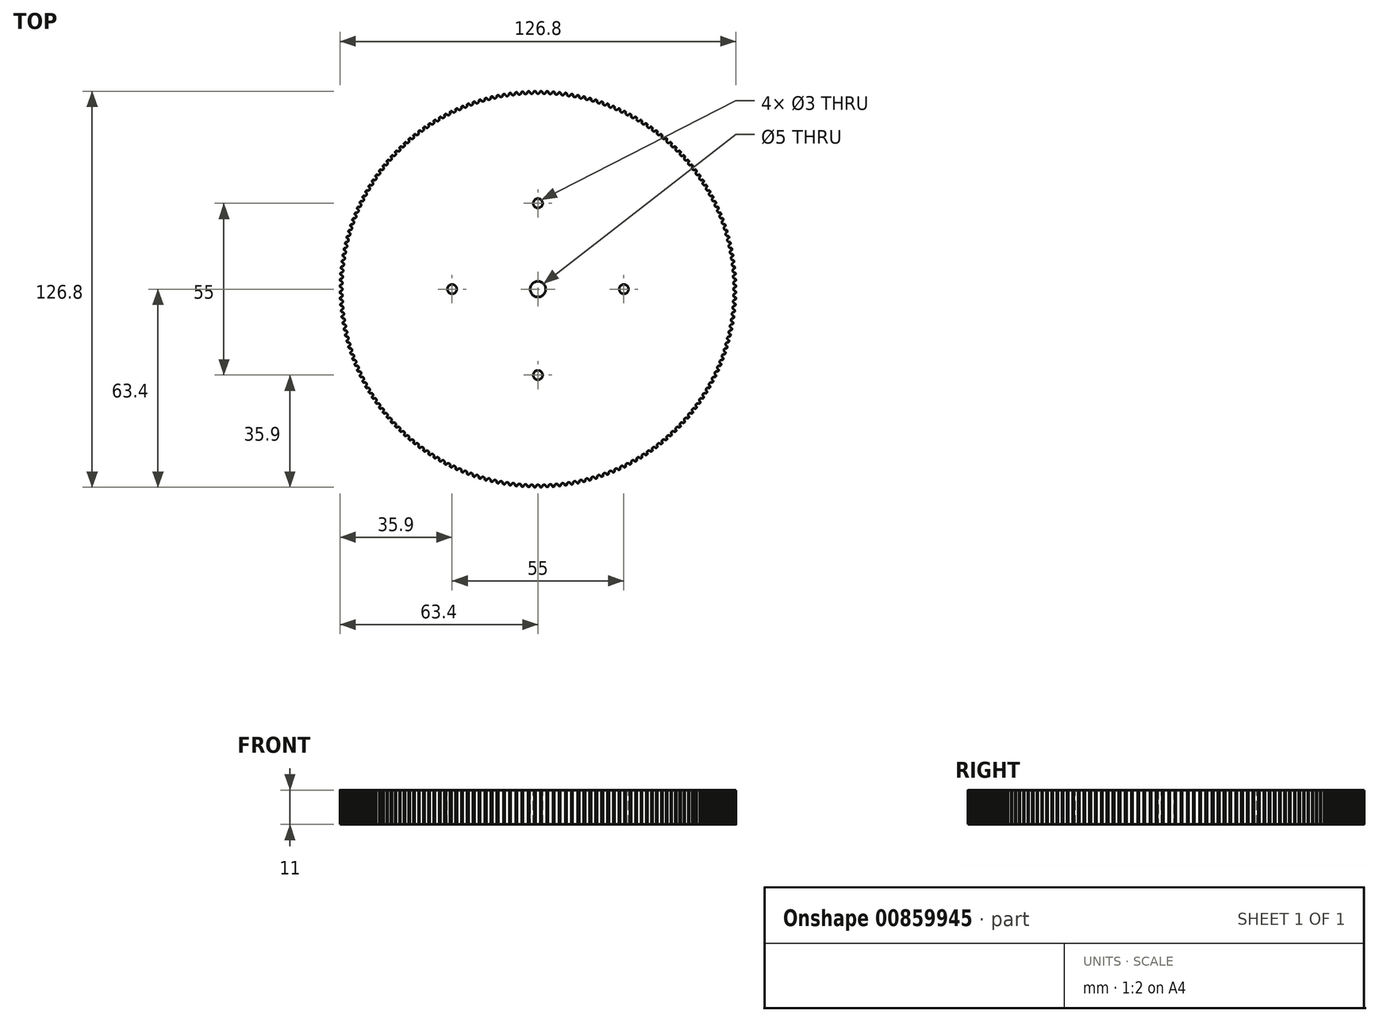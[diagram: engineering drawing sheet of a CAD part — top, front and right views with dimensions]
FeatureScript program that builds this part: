
annotation { "Feature Type Name" : "Feature", "Feature Type Description" : "" }
export const myFeature = defineFeature(function(context is Context, id is Id, definition is map)
    precondition{}
    {
        {
            assignVariable(context, id + "F0", {"name" : "Teeth", "anyValue" : 200});
        }
        {
            var Q0;
            Q0=qCreatedBy(makeId("Top.planeOp"),FACE);
            var sketch = newSketch(context, id + "F1", { "sketchPlane" : qUnion([Q0])});
            skCircle(sketch, "E0", {"center": v(0, 0) * mm, "radius": 63.4 * mm});
            skSolve(sketch);
        }
        {
            var Q0;
            Q0=qCreatedBy(makeId("Top.planeOp"),FACE);
            var sketch = newSketch(context, id + "F2", { "sketchPlane" : qUnion([Q0])});
            skArc(sketch, "E1.0", {"start": v(0.8, 63.4) * mm, "mid": v(0, 63.4) * mm, "end": v(-0.8, 63.4) * mm});
            skLineSegment(sketch, "E2", {"start": v(0, 0) * mm, "end": v(0, 63.23) * mm, "construction": true});
            skArc(sketch, "E3", {"start": v(0, 62.62) * mm, "mid": v(-0.38, 62.76) * mm, "end": v(-0.6, 63.1) * mm});
            skArc(sketch, "E4", {"start": v(-0.6, 63.1) * mm, "mid": v(-0.63, 63.2) * mm, "end": v(-0.68, 63.3) * mm});
            skArc(sketch, "E5", {"start": v(-0.67, 63.3) * mm, "mid": v(-0.73, 63.37) * mm, "end": v(-0.8, 63.4) * mm});
            skArc(sketch, "E6.MirrorCS", {"start": v(0, 62.62) * mm, "mid": v(0.38, 62.76) * mm, "end": v(0.6, 63.1) * mm});
            skArc(sketch, "E7.MirrorCS", {"start": v(0.67, 63.3) * mm, "mid": v(0.73, 63.37) * mm, "end": v(0.8, 63.4) * mm});
            skArc(sketch, "E8.MirrorCS", {"start": v(0.6, 63.1) * mm, "mid": v(0.63, 63.2) * mm, "end": v(0.68, 63.3) * mm});
            skSolve(sketch);
        }
        {
            var Q0;
            Q0=qSketchRegion(id+"F1",true);
            extrude(context, id + "F3", {"entities" : qUnion([Q0]), "depth" : 11 * mm, "offsetDistance" : 25 * mm});
        }
        {
            var Q0;
            Q0=makeQuery(id+"F2.imprint","IMPRINT",FACE,{"disambiguationData":[TD([[makeQuery(id+"F2.imprint","IMPRINT",EDGE,{"derivedFrom":sQuery(id+"F2.wireOp",EDGE,"E1.0")}),1.0]])]});
            extrude(context, id + "F4", {"entities" : qUnion([Q0]), "depth" : 25 * mm, "offsetDistance" : 25 * mm});
        }
        {
            var Q0;
            Q0=makeQuery(id+"F4.opExtrude","SWEPT_BODY",BODY,{"disambiguationData":[OSD([sQuery(id+"F2.wireOp",EDGE,"E1.0"),sQuery(id+"F2.wireOp",EDGE,"E3"),sQuery(id+"F2.wireOp",EDGE,"E4"),sQuery(id+"F2.wireOp",EDGE,"E5"),sQuery(id+"F2.wireOp",EDGE,"E6.MirrorCS"),sQuery(id+"F2.wireOp",EDGE,"E7.MirrorCS"),sQuery(id+"F2.wireOp",EDGE,"E8.MirrorCS")])]});
            var Q1;
            Q1=sQuery(id+"F1.wireOp",EDGE,"E0");
            circularPattern(context, id + "F5", {"operationType" : NewBodyOperationType.REMOVE, "entities" : qUnion([Q0]), "axis" : qUnion([Q1]), "angle" : 360 * degree, "instanceCount" : getVariable(context, 'Teeth'), "equalSpace" : true});
        }
        {
            var Q0;
            Q0=qCreatedBy(makeId("Top.planeOp"),FACE);
            var sketch = newSketch(context, id + "F6", { "sketchPlane" : qUnion([Q0])});
            skCircle(sketch, "E9", {"center": v(0, 0) * mm, "radius": 2.5 * mm});
            skSolve(sketch);
        }
        {
            var Q0;
            Q0=qSketchRegion(id+"F6",true);
            var Q1;
            Q1=sQuery(id+"F6.wireOp",EDGE,"E9");
            extrude(context, id + "F7", {"entities" : qUnion([Q0]), "operationType" : NewBodyOperationType.REMOVE, "surfaceEntities" : qUnion([Q1]), "endBound" : BoundingType.THROUGH_ALL, "depth" : 25 * mm, "offsetDistance" : 25 * mm});
        }
        {
            var Q0;
            Q0=qCreatedBy(makeId("Top.planeOp"),FACE);
            var sketch = newSketch(context, id + "F8", { "sketchPlane" : qUnion([Q0])});
            skCircle(sketch, "E10", {"center": v(0, 0) * mm, "radius": 64.4 * mm});
            skCircle(sketch, "E11.0", {"center": v(0, 0) * mm, "radius": 2.5 * mm});
            skCircle(sketch, "E12.0", {"center": v(0, 0) * mm, "radius": 65.4 * mm});
            skSolve(sketch);
        }
        {
            var Q0;
            Q0=makeQuery(id+"F3.opExtrude","CAP_FACE",FACE,{"disambiguationData":[OSD([sQuery(id+"F1.wireOp",EDGE,"E0")])],"isStart":false});
            var sketch = newSketch(context, id + "F9", { "sketchPlane" : qUnion([Q0])});
            skLineSegment(sketch, "E13", {"start": v(0, 0) * mm, "end": v(0, 27.5) * mm, "construction": true});
            skLineSegment(sketch, "E14", {"start": v(0, 0) * mm, "end": v(27.5, 0) * mm, "construction": true});
            skLineSegment(sketch, "E15", {"start": v(0, 0) * mm, "end": v(0, -27.5) * mm, "construction": true});
            skLineSegment(sketch, "E16", {"start": v(0, 0) * mm, "end": v(-27.5, 0) * mm, "construction": true});
            skCircle(sketch, "E17", {"center": v(0, 27.5) * mm, "radius": 1.5 * mm});
            skCircle(sketch, "E18", {"center": v(-27.5, 0) * mm, "radius": 1.5 * mm});
            skCircle(sketch, "E19", {"center": v(27.5, 0) * mm, "radius": 1.5 * mm});
            skCircle(sketch, "E20", {"center": v(0, -27.5) * mm, "radius": 1.5 * mm});
            skSolve(sketch);
        }
        {
            var Q0;
            Q0=makeQuery(id+"F6.imprint","IMPRINT",FACE,{"disambiguationData":[TD([[makeQuery(id+"F6.imprint","IMPRINT",EDGE,{"derivedFrom":sQuery(id+"F6.wireOp",EDGE,"E9")}),1.0]])]});
            extrude(context, id + "F10", {"entities" : qUnion([Q0]), "operationType" : NewBodyOperationType.REMOVE, "endBound" : BoundingType.THROUGH_ALL, "oppositeDirection" : true, "depth" : 25 * mm, "offsetDistance" : 25 * mm});
        }
        {
            var Q0;
            Q0=qSketchRegion(id+"F9",true);
            extrude(context, id + "F11", {"entities" : qUnion([Q0]), "operationType" : NewBodyOperationType.REMOVE, "endBound" : BoundingType.THROUGH_ALL, "oppositeDirection" : true, "depth" : 25 * mm, "offsetDistance" : 25 * mm});
        }
    });
